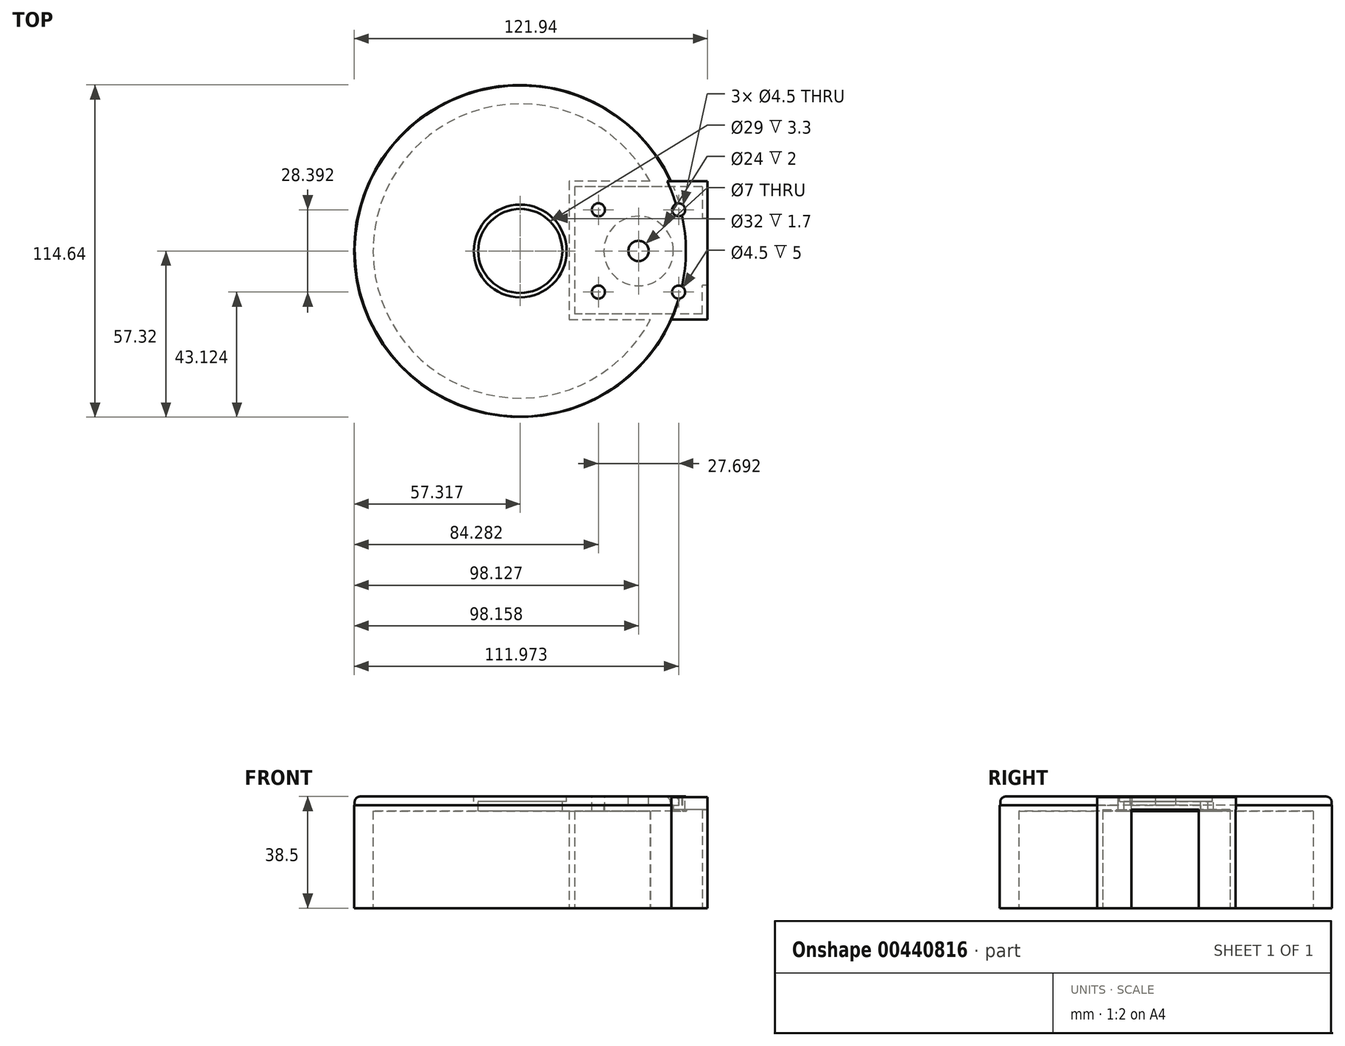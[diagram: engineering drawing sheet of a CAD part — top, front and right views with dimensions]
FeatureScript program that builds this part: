
annotation { "Feature Type Name" : "Feature", "Feature Type Description" : "" }
export const myFeature = defineFeature(function(context is Context, id is Id, definition is map)
    precondition{}
    {
        {
            var Q0;
            Q0=qCreatedBy(makeId("Top.planeOp"),FACE);
            var sketch = newSketch(context, id + "F0", { "sketchPlane" : qUnion([Q0])});
            skLineSegment(sketch, "E0.bottom", {"start": v(76.2, 63.5) * mm, "end": v(-76.2, 63.5) * mm});
            skLineSegment(sketch, "E0.top", {"start": v(76.2, -63.5) * mm, "end": v(-76.2, -63.5) * mm});
            skLineSegment(sketch, "E0.left", {"start": v(76.2, 63.5) * mm, "end": v(76.2, -63.5) * mm});
            skLineSegment(sketch, "E0.right", {"start": v(-76.2, 63.5) * mm, "end": v(-76.2, -63.5) * mm});
            skCircle(sketch, "E1", {"center": v(-17.47, 0) * mm, "radius": 50.8 * mm});
            skCircle(sketch, "E2", {"center": v(-17.47, 0) * mm, "radius": 57.32 * mm});
            skLineSegment(sketch, "E3.bottom", {"start": v(41.23, 11.35) * mm, "end": v(32.01, 11.35) * mm});
            skLineSegment(sketch, "E3.top", {"start": v(41.23, -11.35) * mm, "end": v(32.01, -11.35) * mm});
            skLineSegment(sketch, "E3.left", {"start": v(41.23, 11.35) * mm, "end": v(41.23, -11.35) * mm});
            skLineSegment(sketch, "E3.right", {"start": v(32.01, 11.35) * mm, "end": v(32.01, -11.35) * mm});
            skPoint(sketch, "E3.middle", {"position": v(36.62, 0) * mm});
            skPoint(sketch, "E4.middle", {"position": v(23.33, 0.18) * mm});
            skLineSegment(sketch, "E5.bottom", {"start": v(45.33, 22.18) * mm, "end": v(1.33, 22.18) * mm});
            skLineSegment(sketch, "E5.top", {"start": v(45.33, -21.82) * mm, "end": v(1.33, -21.82) * mm});
            skLineSegment(sketch, "E5.right", {"start": v(1.33, 22.18) * mm, "end": v(1.33, -21.82) * mm});
            skLineSegment(sketch, "E6", {"start": v(45.33, 22.18) * mm, "end": v(45.33, 11.34) * mm});
            skLineSegment(sketch, "E7", {"start": v(45.33, -21.82) * mm, "end": v(45.33, -11.91) * mm});
            skLineSegment(sketch, "E8", {"start": v(45.33, 11.34) * mm, "end": v(47.15, 11.34) * mm});
            skLineSegment(sketch, "E9", {"start": v(47.15, 11.34) * mm, "end": v(47.15, 22.18) * mm});
            skLineSegment(sketch, "E10", {"start": v(47.15, 22.18) * mm, "end": v(47.15, 24.07) * mm});
            skLineSegment(sketch, "E11", {"start": v(47.15, 24.07) * mm, "end": v(1.33, 24.07) * mm});
            skLineSegment(sketch, "E12", {"start": v(1.33, 24.07) * mm, "end": v(-0.63, 24.07) * mm});
            skLineSegment(sketch, "E13", {"start": v(-0.63, 24.07) * mm, "end": v(-0.63, -21.82) * mm});
            skLineSegment(sketch, "E14", {"start": v(-0.63, -21.82) * mm, "end": v(-0.63, -23.73) * mm});
            skLineSegment(sketch, "E15", {"start": v(-0.63, -23.73) * mm, "end": v(45.33, -23.73) * mm});
            skLineSegment(sketch, "E16", {"start": v(45.33, -23.73) * mm, "end": v(47.15, -23.73) * mm});
            skLineSegment(sketch, "E17", {"start": v(47.15, -23.73) * mm, "end": v(47.15, -11.91) * mm});
            skLineSegment(sketch, "E18", {"start": v(47.15, -11.91) * mm, "end": v(45.33, -11.91) * mm});
            skSolve(sketch);
        }
        {
            var Q0;
            {var subQ0=sQuery(id+"F0.wireOp",EDGE,"E11");var subQ1=sQuery(id+"F0.wireOp",EDGE,"E1");var subQ2=makeQuery(id+"F0.imprint","INTERSECT",VERTEX,{"derivedFrom":[subQ1,subQ0]});Q0=makeQuery(id+"F0.imprint","IMPRINT",FACE,{"disambiguationData":[TD([[makeQuery(id+"F0.imprint","IMPRINT",EDGE,{"disambiguationData":[TD([[subQ2,-1.0]])],"derivedFrom":subQ1}),-1.0]])]});}
            var Q1;
            {var subQ0=sQuery(id+"F0.wireOp",EDGE,"E15");var subQ1=sQuery(id+"F0.wireOp",EDGE,"E1");var subQ2=makeQuery(id+"F0.imprint","INTERSECT",VERTEX,{"derivedFrom":[subQ1,subQ0]});Q1=makeQuery(id+"F0.imprint","IMPRINT",FACE,{"disambiguationData":[TD([[makeQuery(id+"F0.imprint","IMPRINT",EDGE,{"disambiguationData":[TD([[subQ2,-1.0]])],"derivedFrom":subQ1}),-1.0]])]});}
            var Q2;
            {var subQ0=sQuery(id+"F0.wireOp",EDGE,"E5.bottom");var subQ1=sQuery(id+"F0.wireOp",EDGE,"E1");var subQ2=makeQuery(id+"F0.imprint","INTERSECT",VERTEX,{"derivedFrom":[subQ1,subQ0]});Q2=makeQuery(id+"F0.imprint","IMPRINT",FACE,{"disambiguationData":[TD([[makeQuery(id+"F0.imprint","IMPRINT",EDGE,{"disambiguationData":[TD([[subQ2,-1.0]])],"derivedFrom":subQ1}),-1.0]])]});}
            extrude(context, id + "F1", {"entities" : qUnion([Q0, Q1, Q2]), "depth" : 33.5 * mm});
        }
        {
            var Q0;
            Q0=makeQuery(id+"F0.imprint","IMPRINT",FACE,{"disambiguationData":[TD([[makeQuery(id+"F0.imprint","IMPRINT",EDGE,{"derivedFrom":sQuery(id+"F0.wireOp",EDGE,"zfkboqaa-8MwC-6LKU-k2ox-AELrlD0kad20.bottom")}),-1.0]])]});
            var Q1;
            {var subQ0=sQuery(id+"F0.wireOp",EDGE,"E5.right");Q1=makeQuery(id+"F0.imprint","IMPRINT",FACE,{"disambiguationData":[TD([[makeQuery(id+"F0.imprint","IMPRINT",EDGE,{"derivedFrom":subQ0}),-1.0]])]});}
            var Q2;
            {var subQ5=sQuery(id+"F0.wireOp",EDGE,"E6");Q2=makeQuery(id+"F0.imprint","IMPRINT",FACE,{"disambiguationData":[TD([[makeQuery(id+"F0.imprint","IMPRINT",EDGE,{"derivedFrom":subQ5}),1.0]])]});}
            var Q3;
            {var subQ4=sQuery(id+"F0.wireOp",EDGE,"E7");Q3=makeQuery(id+"F0.imprint","IMPRINT",FACE,{"disambiguationData":[TD([[makeQuery(id+"F0.imprint","IMPRINT",EDGE,{"derivedFrom":subQ4}),-1.0]])]});}
            extrude(context, id + "F2", {"entities" : qUnion([Q0, Q1, Q2, Q3]), "operationType" : NewBodyOperationType.ADD, "depth" : 34 * mm});
        }
        {
            var Q0;
            Q0=makeQuery(id+"F1.opExtrude","CAP_FACE",FACE,{"disambiguationData":[OSD([sQuery(id+"F0.wireOp",EDGE,"E1"),sQuery(id+"F0.wireOp",EDGE,"E2"),sQuery(id+"F0.wireOp",EDGE,"E3.bottom"),sQuery(id+"F0.wireOp",EDGE,"E3.top")])],"isStart":false});
            var sketch = newSketch(context, id + "F3", { "sketchPlane" : qUnion([Q0])});
            skCircle(sketch, "E19", {"center": v(-17.47, 0) * mm, "radius": 57.32 * mm});
            skCircle(sketch, "E20", {"center": v(23.37, 0) * mm, "radius": 12 * mm});
            skSolve(sketch);
        }
        {
            var Q0;
            Q0 = qSketchRegion(id + "F3", true);
            extrude(context, id + "F4", {"entities" : qUnion([Q0]), "operationType" : NewBodyOperationType.ADD, "depth" : 2 * mm});
        }
        {
            var Q0;
            Q0=makeQuery(id+"F4.opExtrude","CAP_FACE",FACE,{"disambiguationData":[OSD([sQuery(id+"F3.wireOp",EDGE,"E19"),sQuery(id+"F3.wireOp",EDGE,"E20")])],"isStart":false});
            var sketch = newSketch(context, id + "F5", { "sketchPlane" : qUnion([Q0])});
            skCircle(sketch, "E21", {"center": v(-17.47, 0) * mm, "radius": 57.15 * mm});
            skSolve(sketch);
        }
        {
            var Q0;
            Q0=makeQuery(id+"F5.imprint","IMPRINT",FACE,{"disambiguationData":[TD([[makeQuery(id+"F5.imprint","IMPRINT",EDGE,{"derivedFrom":sQuery(id+"F5.wireOp",EDGE,"E21")}),1.0]])]});
            var Q1;
            Q1=makeQuery(id+"F5.imprint","IMPRINT",FACE,{"disambiguationData":[TD([[makeQuery(id+"F5.imprint","IMPRINT",EDGE,{"derivedFrom":makeQuery(id+"F4.opExtrude","CAP_EDGE",EDGE,{"disambiguationData":[OSD([sQuery(id+"F3.wireOp",EDGE,"E20")])],"isStart":false})}),1.0]])]});
            extrude(context, id + "F6", {"entities" : qUnion([Q0, Q1]), "operationType" : NewBodyOperationType.ADD, "depth" : 3 * mm});
        }
        {
            var Q0;
            Q0=makeQuery(id+"F6.opExtrude","CAP_FACE",FACE,{"disambiguationData":[OSD([sQuery(id+"F5.wireOp",EDGE,"E21")])],"isStart":false});
            var sketch = newSketch(context, id + "F7", { "sketchPlane" : qUnion([Q0])});
            skCircle(sketch, "E22", {"center": v(23.34, 0) * mm, "radius": 3.5 * mm});
            skSolve(sketch);
        }
        {
            var Q0;
            Q0=makeQuery(id+"F7.imprint","IMPRINT",FACE,{"disambiguationData":[TD([[makeQuery(id+"F7.imprint","IMPRINT",EDGE,{"derivedFrom":sQuery(id+"F7.wireOp",EDGE,"E22")}),1.0]])]});
            extrude(context, id + "F8", {"entities" : qUnion([Q0]), "operationType" : NewBodyOperationType.REMOVE, "oppositeDirection" : true, "depth" : 3 * mm});
        }
        {
            var Q0;
            Q0=makeQuery(id+"F2.opExtrude","CAP_FACE",FACE,{"disambiguationData":[OSD([sQuery(id+"F0.wireOp",EDGE,"E2"),sQuery(id+"F0.wireOp",EDGE,"E5.top"),sQuery(id+"F0.wireOp",EDGE,"E7"),sQuery(id+"F0.wireOp",EDGE,"E15"),sQuery(id+"F0.wireOp",EDGE,"E16"),sQuery(id+"F0.wireOp",EDGE,"E17"),sQuery(id+"F0.wireOp",EDGE,"E18")])],"isStart":false});
            var sketch = newSketch(context, id + "F9", { "sketchPlane" : qUnion([Q0])});
            skArc(sketch, "E23", {"start": v(34.7, -23.73) * mm, "mid": v(39.58, 0.25) * mm, "end": v(34.28, 24.14) * mm});
            skLineSegment(sketch, "E24", {"start": v(47.15, -23.73) * mm, "end": v(34.7, -23.73) * mm});
            skLineSegment(sketch, "E25", {"start": v(47.15, -23.73) * mm, "end": v(47.15, 24.14) * mm});
            skLineSegment(sketch, "E26", {"start": v(47.15, 24.14) * mm, "end": v(34.28, 24.14) * mm});
            skSolve(sketch);
        }
        {
            var Q0;
            Q0 = qSketchRegion(id + "F9", true);
            extrude(context, id + "F10", {"entities" : qUnion([Q0]), "operationType" : NewBodyOperationType.ADD, "depth" : 4.32 * mm});
        }
        {
            var Q0;
            Q0=makeQuery(id+"F6.opExtrude","CAP_FACE",FACE,{"disambiguationData":[OSD([sQuery(id+"F5.wireOp",EDGE,"E21")])],"isStart":false});
            var sketch = newSketch(context, id + "F11", { "sketchPlane" : qUnion([Q0])});
            skCircle(sketch, "E27", {"center": v(-17.47, 0) * mm, "radius": 14.5 * mm});
            skSolve(sketch);
        }
        {
            var Q0;
            Q0 = qSketchRegion(id + "F11", true);
            extrude(context, id + "F12", {"entities" : qUnion([Q0]), "operationType" : NewBodyOperationType.REMOVE, "oppositeDirection" : true, "depth" : 25.4 * mm});
        }
        {
            var Q0;
            Q0=makeQuery(id+"F6.opExtrude","CAP_FACE",FACE,{"disambiguationData":[OSD([sQuery(id+"F5.wireOp",EDGE,"E21")])],"isStart":false});
            var sketch = newSketch(context, id + "F13", { "sketchPlane" : qUnion([Q0])});
            skCircle(sketch, "E28", {"center": v(-17.47, 0) * mm, "radius": 16 * mm});
            skSolve(sketch);
        }
        {
            var Q0;
            Q0 = qSketchRegion(id + "F13", true);
            extrude(context, id + "F14", {"entities" : qUnion([Q0]), "operationType" : NewBodyOperationType.REMOVE, "oppositeDirection" : true, "depth" : 1.7 * mm});
        }
        {
            var Q0;
            Q0=makeQuery(id+"F6.opExtrude","CAP_FACE",FACE,{"disambiguationData":[OSD([sQuery(id+"F5.wireOp",EDGE,"E21")])],"isStart":false});
            var sketch = newSketch(context, id + "F15", { "sketchPlane" : qUnion([Q0])});
            skLineSegment(sketch, "E29", {"start": v(9.5, 22.2) * mm, "end": v(9.5, 14.2) * mm});
            skLineSegment(sketch, "E30", {"start": v(9.5, 14.2) * mm, "end": v(1.5, 14.2) * mm});
            skCircle(sketch, "E31", {"center": v(9.5, 14.2) * mm, "radius": 2.25 * mm});
            skLineSegment(sketch, "E32.MirrorCS", {"start": v(9.5, -22.2) * mm, "end": v(9.5, -14.2) * mm});
            skLineSegment(sketch, "E33.MirrorCS", {"start": v(9.5, -14.2) * mm, "end": v(1.5, -14.2) * mm});
            skCircle(sketch, "E34.MirrorC", {"center": v(9.5, -14.2) * mm, "radius": 2.25 * mm});
            skLineSegment(sketch, "E35", {"start": v(23.34, 0) * mm, "end": v(23.34, 24.28) * mm});
            skLineSegment(sketch, "E36", {"start": v(23.34, 24.28) * mm, "end": v(23.34, -24.11) * mm});
            skLineSegment(sketch, "E37.MirrorCS", {"start": v(37.18, 22.2) * mm, "end": v(37.18, 14.2) * mm});
            skLineSegment(sketch, "E38.MirrorCS", {"start": v(37.18, 14.2) * mm, "end": v(45.18, 14.2) * mm});
            skCircle(sketch, "E39.MirrorC", {"center": v(37.18, 14.2) * mm, "radius": 2.25 * mm});
            skLineSegment(sketch, "E40.MirrorCS", {"start": v(37.18, -14.2) * mm, "end": v(45.18, -14.2) * mm});
            skLineSegment(sketch, "E41.MirrorCS", {"start": v(37.18, -22.2) * mm, "end": v(37.18, -14.2) * mm});
            skCircle(sketch, "E42.MirrorC", {"center": v(37.18, -14.2) * mm, "radius": 2.25 * mm});
            skSolve(sketch);
        }
        {
            var Q0;
            Q0 = qSketchRegion(id + "F15", true);
            extrude(context, id + "F16", {"entities" : qUnion([Q0]), "operationType" : NewBodyOperationType.REMOVE, "oppositeDirection" : true, "depth" : 25.4 * mm});
        }
        {
            var Q0;
            Q0=makeQuery(id+"F16.boolean.opBoolean","SPLIT",EDGE,{"disambiguationData":[OD(0.0)],"derivedFrom":makeQuery(id+"F6.opExtrude","CAP_EDGE",EDGE,{"disambiguationData":[OSD([sQuery(id+"F5.wireOp",EDGE,"E21")])],"isStart":false})});
            fillet(context, id + "F17", {"entities" : qUnion([Q0]), "radius" : 1.84 * mm, "tangentPropagation" : true, "allowEdgeOverflow" : false});
        }
    });
